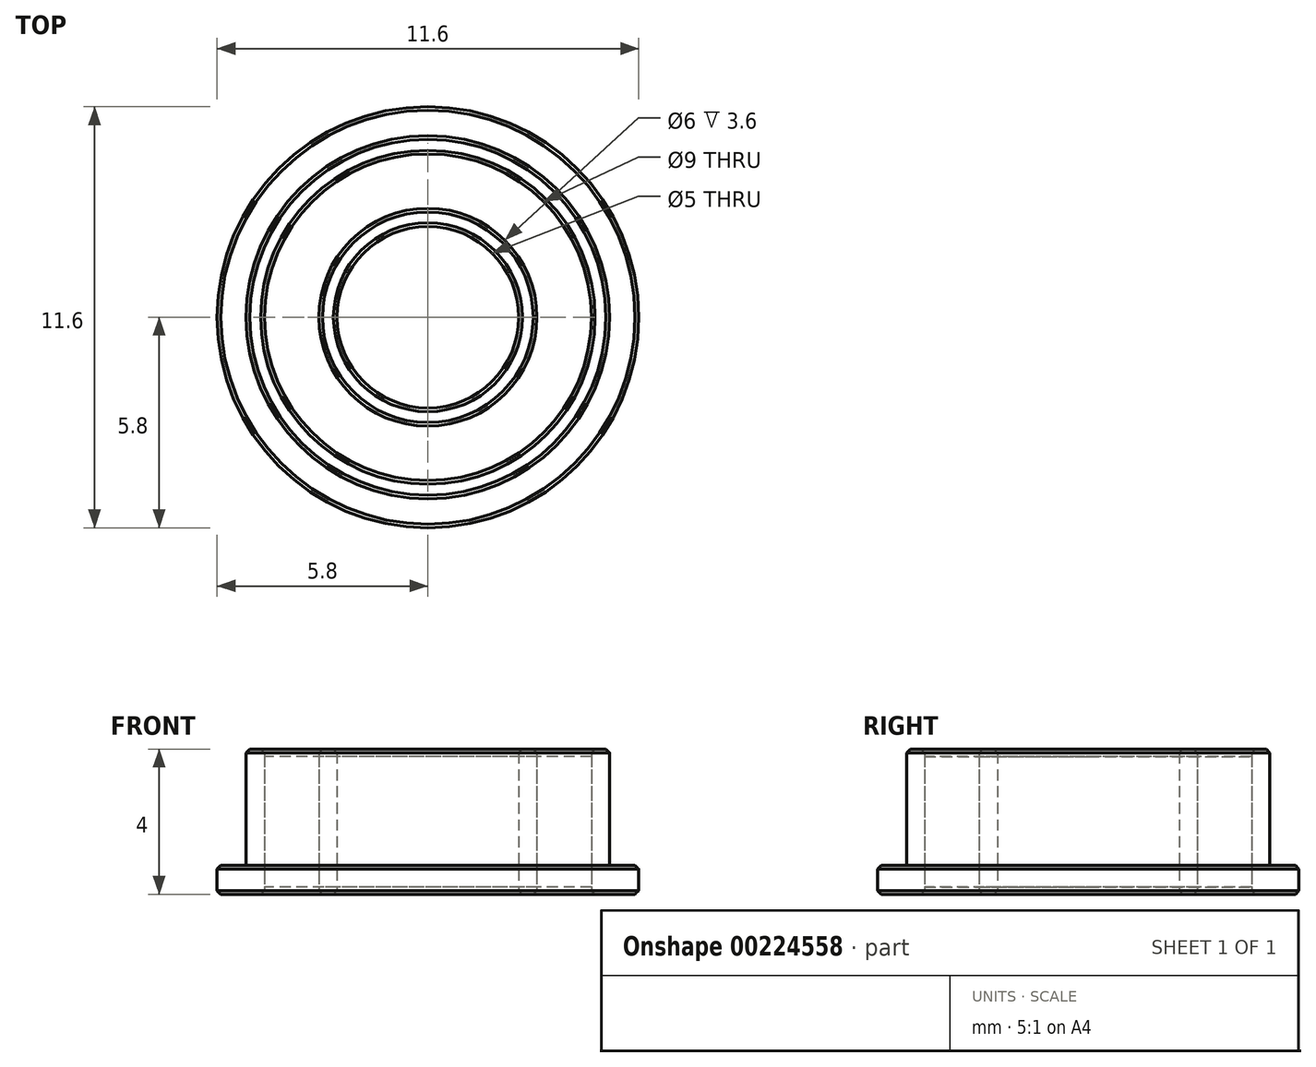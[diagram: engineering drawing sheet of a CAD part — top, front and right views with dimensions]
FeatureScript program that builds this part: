
annotation { "Feature Type Name" : "Feature", "Feature Type Description" : "" }
export const myFeature = defineFeature(function(context is Context, id is Id, definition is map)
    precondition{}
    {
        {
            var Q0;
            Q0=qCreatedBy(makeId("Top.planeOp"),FACE);
            var sketch = newSketch(context, id + "F0", { "sketchPlane" : qUnion([Q0])});
            skCircle(sketch, "E0", {"center": v(0, 0) * mm, "radius": 5.8 * mm});
            skCircle(sketch, "E1", {"center": v(0, 0) * mm, "radius": 5 * mm});
            skCircle(sketch, "E2", {"center": v(0, 0) * mm, "radius": 2.5 * mm});
            skCircle(sketch, "E3.0", {"center": v(0, 0) * mm, "radius": 4.5 * mm});
            skCircle(sketch, "E4.0", {"center": v(0, 0) * mm, "radius": 3 * mm});
            skSolve(sketch);
        }
        {
            var Q0;
            Q0=makeQuery(id+"F0.imprint","IMPRINT",FACE,{"disambiguationData":[TD([[makeQuery(id+"F0.imprint","IMPRINT",EDGE,{"derivedFrom":sQuery(id+"F0.wireOp",EDGE,"E2")}),-1.0]])]});
            var Q1;
            Q1=makeQuery(id+"F0.imprint","IMPRINT",FACE,{"disambiguationData":[TD([[makeQuery(id+"F0.imprint","IMPRINT",EDGE,{"derivedFrom":sQuery(id+"F0.wireOp",EDGE,"E1")}),1.0]])]});
            extrude(context, id + "F1", {"entities" : qUnion([Q0, Q1]), "depth" : 4 * mm});
        }
        {
            var Q0;
            Q0=makeQuery(id+"F0.imprint","IMPRINT",FACE,{"disambiguationData":[TD([[makeQuery(id+"F0.imprint","IMPRINT",EDGE,{"derivedFrom":sQuery(id+"F0.wireOp",EDGE,"E0")}),1.0]])]});
            extrude(context, id + "F2", {"entities" : qUnion([Q0]), "operationType" : NewBodyOperationType.ADD, "depth" : 0.8 * mm});
        }
        {
            var Q0;
            Q0=makeQuery(id+"F0.imprint","IMPRINT",FACE,{"disambiguationData":[TD([[makeQuery(id+"F0.imprint","IMPRINT",EDGE,{"derivedFrom":sQuery(id+"F0.wireOp",EDGE,"E3.0")}),1.0]])]});
            extrude(context, id + "F3", {"entities" : qUnion([Q0]), "depth" : 3.8 * mm, "hasSecondDirection" : true, "secondDirectionOppositeDirection" : false, "secondDirectionDepth" : 0.2 * mm});
        }
        {
            var Q0;
            {var subQ0=sQuery(id+"F0.wireOp",EDGE,"E1");Q0=makeQuery(id+"F2.boolean.opBoolean","MERGE",FACE,{"derivedFrom":[makeQuery(id+"F1.opExtrude","CAP_FACE",FACE,{"disambiguationData":[OSD([subQ0,sQuery(id+"F0.wireOp",EDGE,"E3.0")])],"isStart":true}),makeQuery(id+"F2.opExtrude","CAP_FACE",FACE,{"disambiguationData":[OSD([sQuery(id+"F0.wireOp",EDGE,"E0"),subQ0])],"isStart":true})]});}
            var Q1;
            Q1=makeQuery(id+"F1.opExtrude","CAP_FACE",FACE,{"disambiguationData":[OSD([sQuery(id+"F0.wireOp",EDGE,"E2"),sQuery(id+"F0.wireOp",EDGE,"E4.0")])],"isStart":true});
            var Q2;
            Q2=makeQuery(id+"F1.opExtrude","CAP_FACE",FACE,{"disambiguationData":[OSD([sQuery(id+"F0.wireOp",EDGE,"E1"),sQuery(id+"F0.wireOp",EDGE,"E3.0")])],"isStart":false});
            var Q3;
            Q3=makeQuery(id+"F1.opExtrude","CAP_FACE",FACE,{"disambiguationData":[OSD([sQuery(id+"F0.wireOp",EDGE,"E2"),sQuery(id+"F0.wireOp",EDGE,"E4.0")])],"isStart":false});
            var Q4;
            Q4=makeQuery(id+"F2.opExtrude","CAP_EDGE",EDGE,{"disambiguationData":[OSD([sQuery(id+"F0.wireOp",EDGE,"E0")])],"isStart":false});
            chamfer(context, id + "F4", {"entities" : qUnion([Q0, Q1, Q2, Q3, Q4]), "width" : 0.1 * mm, "tangentPropagation" : true});
        }
    });
